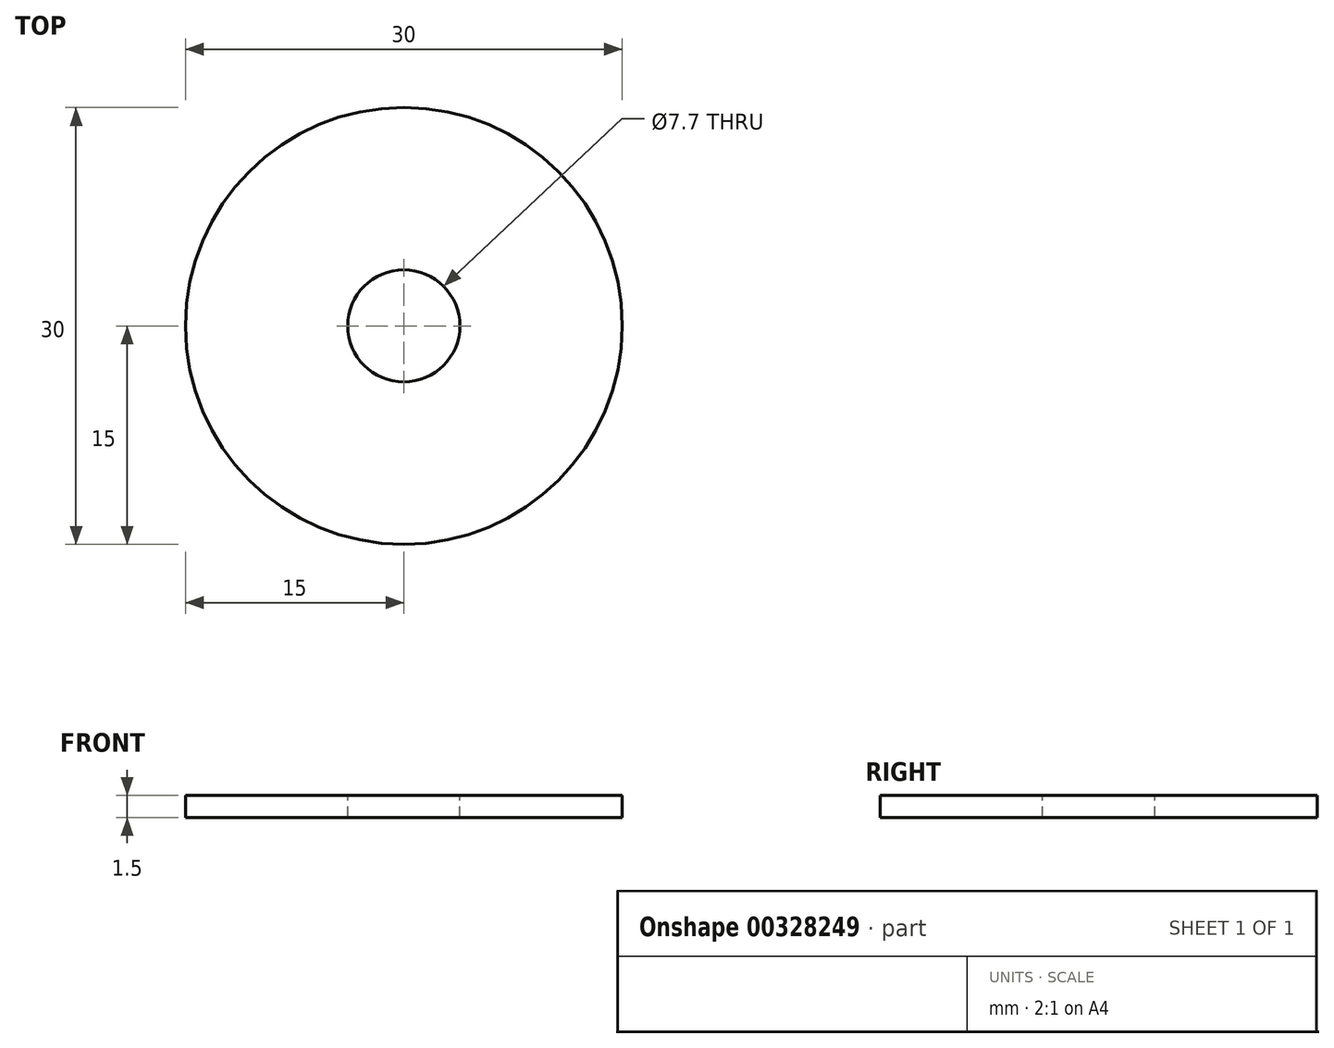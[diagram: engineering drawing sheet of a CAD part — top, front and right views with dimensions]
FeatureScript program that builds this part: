
annotation { "Feature Type Name" : "Feature", "Feature Type Description" : "" }
export const myFeature = defineFeature(function(context is Context, id is Id, definition is map)
    precondition{}
    {
        {
            var Q0;
            Q0=qCreatedBy(makeId("Top.planeOp"),FACE);
            var sketch = newSketch(context, id + "F0", { "sketchPlane" : qUnion([Q0])});
            skCircle(sketch, "E0", {"center": v(0, 0) * mm, "radius": 15 * mm});
            skCircle(sketch, "E1", {"center": v(0, 0) * mm, "radius": 2 * mm});
            skSolve(sketch);
        }
        {
            var Q0;
            Q0=makeQuery(id+"F0.imprint","IMPRINT",FACE,{"disambiguationData":[TD([[makeQuery(id+"F0.imprint","IMPRINT",EDGE,{"derivedFrom":sQuery(id+"F0.wireOp",EDGE,"E0")}),1.0]])]});
            extrude(context, id + "F1", {"entities" : qUnion([Q0]), "depth" : 1.5 * mm});
        }
        {
            var Q0;
            Q0=makeQuery(id+"F1.opExtrude","CAP_FACE",FACE,{"disambiguationData":[OSD([sQuery(id+"F0.wireOp",EDGE,"E0"),sQuery(id+"F0.wireOp",EDGE,"E1")])],"isStart":false});
            var sketch = newSketch(context, id + "F2", { "sketchPlane" : qUnion([Q0])});
            skCircle(sketch, "E2", {"center": v(0, 0) * mm, "radius": 3.85 * mm});
            skSolve(sketch);
        }
        {
            var Q0;
            Q0=makeQuery(id+"F2.imprint","IMPRINT",FACE,{"disambiguationData":[TD([[makeQuery(id+"F2.imprint","IMPRINT",EDGE,{"derivedFrom":sQuery(id+"F2.wireOp",EDGE,"E2")}),1.0]])]});
            extrude(context, id + "F3", {"entities" : qUnion([Q0]), "operationType" : NewBodyOperationType.ADD, "depth" : 11.5 * mm});
        }
        {
            var Q0;
            Q0=makeQuery(id+"F3.opExtrude","CAP_FACE",FACE,{"disambiguationData":[OSD([sQuery(id+"F0.wireOp",EDGE,"E1"),sQuery(id+"F2.wireOp",EDGE,"E2")])],"isStart":false});
            extrude(context, id + "F4", {"entities" : qUnion([Q0]), "operationType" : NewBodyOperationType.REMOVE, "oppositeDirection" : true, "depth" : 25 * mm});
        }
    });
